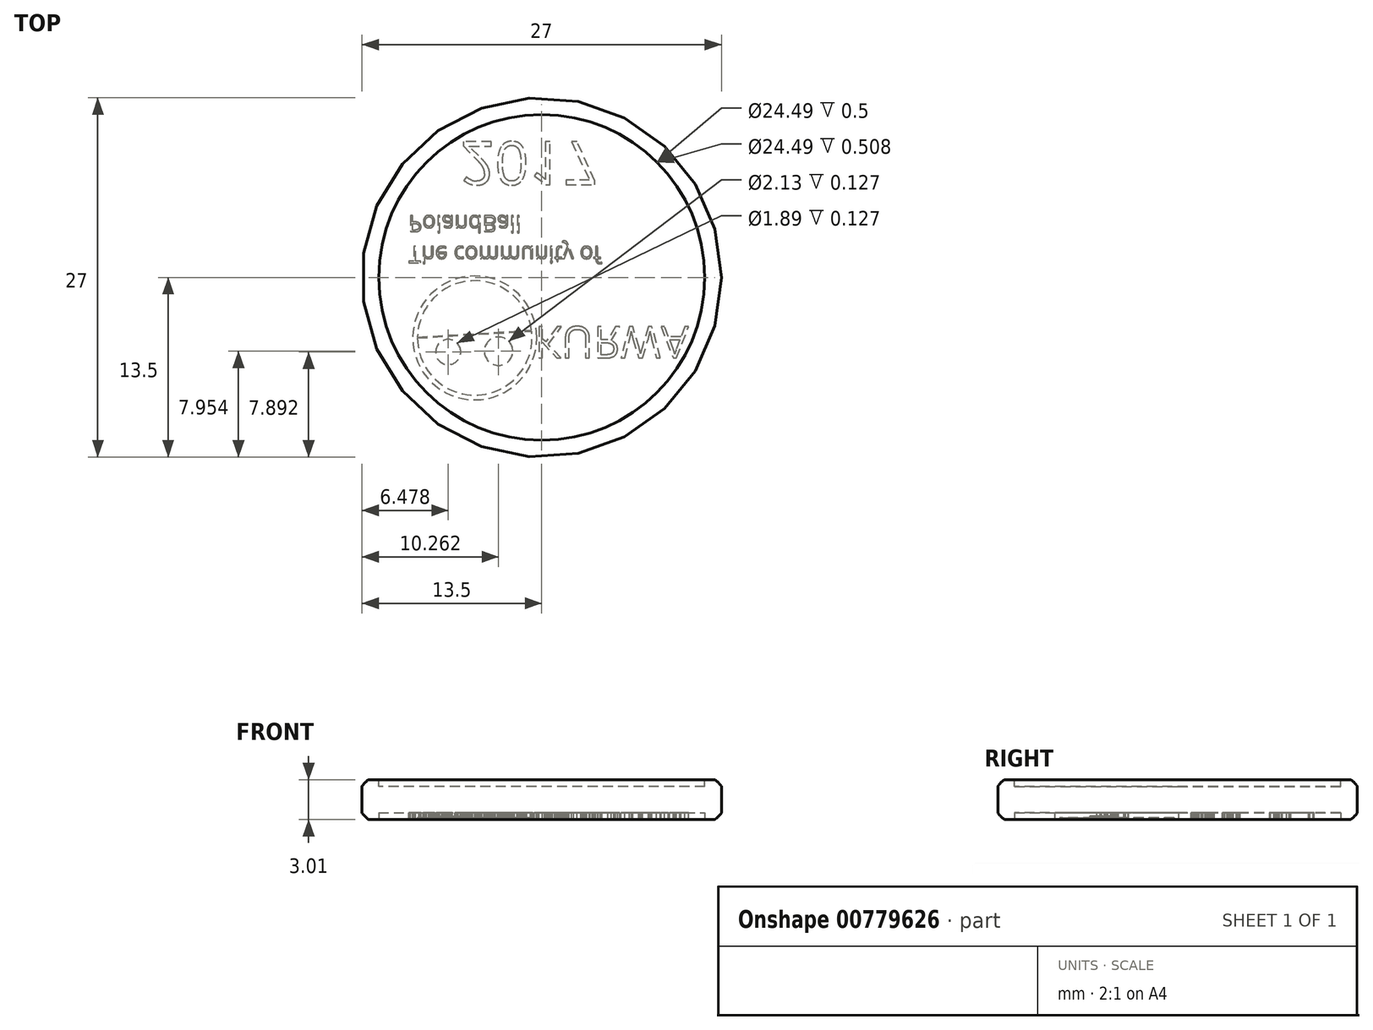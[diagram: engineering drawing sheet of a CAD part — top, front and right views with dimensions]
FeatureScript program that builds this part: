
annotation { "Feature Type Name" : "Feature", "Feature Type Description" : "" }
export const myFeature = defineFeature(function(context is Context, id is Id, definition is map)
    precondition{}
    {
        {
            var Q0;
            Q0=qCreatedBy(makeId("Top.planeOp"),FACE);
            var sketch = newSketch(context, id + "F0", { "sketchPlane" : qUnion([Q0])});
            skCircle(sketch, "E0", {"center": v(0, 0) * mm, "radius": 13.5 * mm});
            skSolve(sketch);
        }
        {
            var Q0;
            Q0=makeQuery(id+"F0.imprint","IMPRINT",FACE,{"disambiguationData":[TD([[makeQuery(id+"F0.imprint","IMPRINT",EDGE,{"derivedFrom":sQuery(id+"F0.wireOp",EDGE,"E0")}),1.0]])]});
            extrude(context, id + "F1", {"entities" : qUnion([Q0]), "depth" : 3 * mm, "offsetDistance" : 25.4 * mm});
        }
        {
            var Q0;
            Q0=makeQuery(id+"F1.opExtrude","CAP_FACE",FACE,{"disambiguationData":[OSD([sQuery(id+"F0.wireOp",EDGE,"E0"),sQuery(id+"F0.wireOp",EDGE,"Qun56cqf-QtSN-Wwvj-NGIt-83J3yqvec6jL")])],"isStart":true});
            var sketch = newSketch(context, id + "F2", { "sketchPlane" : qUnion([Q0])});
            skCircle(sketch, "E1", {"center": v(0, 0) * mm, "radius": 12.25 * mm});
            skSolve(sketch);
        }
        {
            var Q0;
            Q0=makeQuery(id+"F1.opExtrude","CAP_FACE",FACE,{"disambiguationData":[OSD([sQuery(id+"F0.wireOp",EDGE,"E0"),sQuery(id+"F0.wireOp",EDGE,"Qun56cqf-QtSN-Wwvj-NGIt-83J3yqvec6jL")])],"isStart":false});
            var sketch = newSketch(context, id + "F3", { "sketchPlane" : qUnion([Q0])});
            skCircle(sketch, "E2", {"center": v(0, 0) * mm, "radius": 12.25 * mm});
            skSolve(sketch);
        }
        {
            var Q0;
            Q0=makeQuery(id+"F2.imprint","IMPRINT",FACE,{"disambiguationData":[TD([[makeQuery(id+"F2.imprint","IMPRINT",EDGE,{"derivedFrom":sQuery(id+"F2.wireOp",EDGE,"E1")}),1.0]])]});
            extrude(context, id + "F4", {"entities" : qUnion([Q0]), "operationType" : NewBodyOperationType.REMOVE, "oppositeDirection" : true, "depth" : 0.5 * mm, "offsetDistance" : 25.4 * mm});
        }
        {
            var Q0;
            Q0=makeQuery(id+"F3.imprint","IMPRINT",FACE,{"disambiguationData":[TD([[makeQuery(id+"F3.imprint","IMPRINT",EDGE,{"derivedFrom":sQuery(id+"F3.wireOp",EDGE,"E2")}),1.0]])]});
            extrude(context, id + "F5", {"entities" : qUnion([Q0]), "operationType" : NewBodyOperationType.REMOVE, "oppositeDirection" : true, "depth" : 0.5 * mm, "offsetDistance" : 25.4 * mm});
        }
        {
            var Q0;
            Q0=makeQuery(id+"F4.boolean.opBoolean","COPY",FACE,{"derivedFrom":makeQuery(id+"F4.opExtrude","CAP_FACE",FACE,{"disambiguationData":[OSD([sQuery(id+"F0.wireOp",EDGE,"Qun56cqf-QtSN-Wwvj-NGIt-83J3yqvec6jL"),sQuery(id+"F2.wireOp",EDGE,"E1")])],"isStart":false})});
            var sketch = newSketch(context, id + "F6", { "sketchPlane" : qUnion([Q0])});
            skSolve(sketch);
        }
        {
            var Q0;
            Q0=makeQuery(id+"F1.opExtrude","CAP_EDGE",EDGE,{"disambiguationData":[OSD([sQuery(id+"F0.wireOp",EDGE,"E0")])],"isStart":false});
            fillet(context, id + "F7", {"entities" : qUnion([Q0]), "radius" : 0.5 * mm, "rho" : 0.1, "crossSection" : FilletCrossSection.CONIC, "allowEdgeOverflow" : false});
        }
        {
            var Q0;
            Q0=makeQuery(id+"F1.opExtrude","CAP_EDGE",EDGE,{"disambiguationData":[OSD([sQuery(id+"F0.wireOp",EDGE,"E0")])],"isStart":true});
            fillet(context, id + "F8", {"entities" : qUnion([Q0]), "radius" : 0.5 * mm, "rho" : 0.1, "crossSection" : FilletCrossSection.CONIC, "allowEdgeOverflow" : false});
        }
        {
            var Q0;
            Q0=makeQuery(id+"F6.imprint","IMPRINT",FACE,{"disambiguationData":[TD([[makeQuery(id+"F6.imprint","IMPRINT",EDGE,{"derivedFrom":makeQuery(id+"F4.boolean.opBoolean","COPY",EDGE,{"derivedFrom":makeQuery(id+"F4.opExtrude","CAP_EDGE",EDGE,{"disambiguationData":[OSD([sQuery(id+"F2.wireOp",EDGE,"E1")])],"isStart":false})})}),1.0]])]});
            var sketch = newSketch(context, id + "F9", { "sketchPlane" : qUnion([Q0])});
            skCircle(sketch, "E3", {"center": v(-5.03, 4.55) * mm, "radius": 4.66 * mm});
            skSolve(sketch);
        }
        {
            var Q0;
            Q0=makeQuery(id+"F9.imprint","IMPRINT",FACE,{"disambiguationData":[TD([[makeQuery(id+"F9.imprint","IMPRINT",EDGE,{"derivedFrom":sQuery(id+"F9.wireOp",EDGE,"E3")}),1.0]])]});
            extrude(context, id + "F10", {"entities" : qUnion([Q0]), "operationType" : NewBodyOperationType.ADD, "depth" : 0.5 * mm, "offsetDistance" : 25.4 * mm});
        }
        {
            var Q0;
            Q0=makeQuery(id+"F6.imprint","IMPRINT",FACE,{"disambiguationData":[TD([[makeQuery(id+"F6.imprint","IMPRINT",EDGE,{"derivedFrom":makeQuery(id+"F4.boolean.opBoolean","COPY",EDGE,{"derivedFrom":makeQuery(id+"F4.opExtrude","CAP_EDGE",EDGE,{"disambiguationData":[OSD([sQuery(id+"F2.wireOp",EDGE,"E1")])],"isStart":false})})}),1.0]])]});
            var sketch = newSketch(context, id + "F11", { "sketchPlane" : qUnion([Q0])});
            skText(sketch, "E4", { "text": "The community of \nPolandBall", "fontName": "OpenSans-Regular.ttf"});
            const initialGuessF11  = {"E4": [-0.01001, -0.00233, 1, 0, 0.00123]};
            skSetInitialGuess(sketch, initialGuessF11);
            skSolve(sketch);
        }
        {
            var Q0;
            Q0 = qSketchRegion(id + "F11", true);
            extrude(context, id + "F12", {"entities" : qUnion([Q0]), "operationType" : NewBodyOperationType.ADD, "depth" : 0.5 * mm, "offsetDistance" : 25.4 * mm});
        }
        {
            var Q0;
            Q0=makeQuery(id+"F10.opExtrude","CAP_FACE",FACE,{"disambiguationData":[OSD([sQuery(id+"F9.wireOp",EDGE,"E3")])],"isStart":false});
            var sketch = newSketch(context, id + "F13", { "sketchPlane" : qUnion([Q0])});
            skCircle(sketch, "E5", {"center": v(-7.02, 5.6) * mm, "radius": 0.95 * mm});
            skCircle(sketch, "E6", {"center": v(-3.24, 5.55) * mm, "radius": 1.07 * mm});
            skLineSegment(sketch, "E7", {"start": v(-9.69, 4.68) * mm, "end": v(-0.43, 3.81) * mm});
            skSolve(sketch);
        }
        {
            var Q0;
            Q0=makeQuery(id+"F13.imprint","IMPRINT",FACE,{"disambiguationData":[TD([[makeQuery(id+"F13.imprint","IMPRINT",EDGE,{"derivedFrom":sQuery(id+"F13.wireOp",EDGE,"E5")}),1.0]])]});
            var Q1;
            Q1=makeQuery(id+"F13.imprint","IMPRINT",FACE,{"disambiguationData":[TD([[makeQuery(id+"F13.imprint","IMPRINT",EDGE,{"derivedFrom":sQuery(id+"F13.wireOp",EDGE,"E6")}),1.0]])]});
            extrude(context, id + "F14", {"entities" : qUnion([Q0, Q1]), "operationType" : NewBodyOperationType.REMOVE, "oppositeDirection" : true, "depth" : 0.25 * mm, "offsetDistance" : 25.4 * mm});
        }
        {
            var Q0;
            Q0=makeQuery(id+"F10.opExtrude","CAP_FACE",FACE,{"disambiguationData":[OSD([sQuery(id+"F9.wireOp",EDGE,"E3")])],"isStart":false});
            var sketch = newSketch(context, id + "F15", { "sketchPlane" : qUnion([Q0])});
            skCircle(sketch, "E8", {"center": v(-5.03, 4.55) * mm, "radius": 4.3 * mm});
            skLineSegment(sketch, "E9", {"start": v(-9.33, 4.56) * mm, "end": v(-0.76, 4.03) * mm});
            skLineSegment(sketch, "E10", {"start": v(-9.33, 4.48) * mm, "end": v(-0.77, 3.96) * mm});
            skSolve(sketch);
        }
        {
            var Q0;
            {var subQ0=sQuery(id+"F15.wireOp",EDGE,"E9");Q0=makeQuery(id+"F15.imprint","IMPRINT",FACE,{"disambiguationData":[TD([[makeQuery(id+"F15.imprint","IMPRINT",EDGE,{"derivedFrom":subQ0}),1.0]])]});}
            var Q1;
            {var subQ0=sQuery(id+"F15.wireOp",EDGE,"E10");Q1=makeQuery(id+"F15.imprint","IMPRINT",FACE,{"disambiguationData":[TD([[makeQuery(id+"F15.imprint","IMPRINT",EDGE,{"derivedFrom":subQ0}),-1.0]])]});}
            extrude(context, id + "F16", {"entities" : qUnion([Q0, Q1]), "operationType" : NewBodyOperationType.REMOVE, "oppositeDirection" : true, "depth" : 0.13 * mm, "offsetDistance" : 25.4 * mm});
        }
        {
            var Q0;
            Q0=makeQuery(id+"F6.imprint","IMPRINT",FACE,{"disambiguationData":[TD([[makeQuery(id+"F6.imprint","IMPRINT",EDGE,{"derivedFrom":makeQuery(id+"F4.boolean.opBoolean","COPY",EDGE,{"derivedFrom":makeQuery(id+"F4.opExtrude","CAP_EDGE",EDGE,{"disambiguationData":[OSD([sQuery(id+"F2.wireOp",EDGE,"E1")])],"isStart":false})})}),1.0]])]});
            var sketch = newSketch(context, id + "F17", { "sketchPlane" : qUnion([Q0])});
            skText(sketch, "E11", { "text": "KURWA", "fontName": "OpenSans-Regular.ttf"});
            const initialGuessF17  = {"E11": [-0.00054, 0.0037, 1, 0, 0.00237]};
            skSetInitialGuess(sketch, initialGuessF17);
            skSolve(sketch);
        }
        {
            var Q0;
            Q0 = qSketchRegion(id + "F17", true);
            extrude(context, id + "F18", {"entities" : qUnion([Q0]), "operationType" : NewBodyOperationType.ADD, "depth" : 0.5 * mm, "offsetDistance" : 25.4 * mm});
        }
        {
            var Q0;
            Q0=makeQuery(id+"F6.imprint","IMPRINT",FACE,{"disambiguationData":[TD([[makeQuery(id+"F6.imprint","IMPRINT",EDGE,{"derivedFrom":makeQuery(id+"F4.boolean.opBoolean","COPY",EDGE,{"derivedFrom":makeQuery(id+"F4.opExtrude","CAP_EDGE",EDGE,{"disambiguationData":[OSD([sQuery(id+"F2.wireOp",EDGE,"E1")])],"isStart":false})})}),1.0]])]});
            var sketch = newSketch(context, id + "F19", { "sketchPlane" : qUnion([Q0])});
            skText(sketch, "E12", { "text": "2017", "fontName": "OpenSans-Regular.ttf"});
            const initialGuessF19  = {"E12": [-0.00612, -0.0102, 1, 0, 0.00325]};
            skSetInitialGuess(sketch, initialGuessF19);
            skSolve(sketch);
        }
        {
            var Q0;
            Q0 = qSketchRegion(id + "F19", true);
            extrude(context, id + "F20", {"entities" : qUnion([Q0]), "operationType" : NewBodyOperationType.ADD, "depth" : 0.5 * mm, "offsetDistance" : 25.4 * mm});
        }
    });
